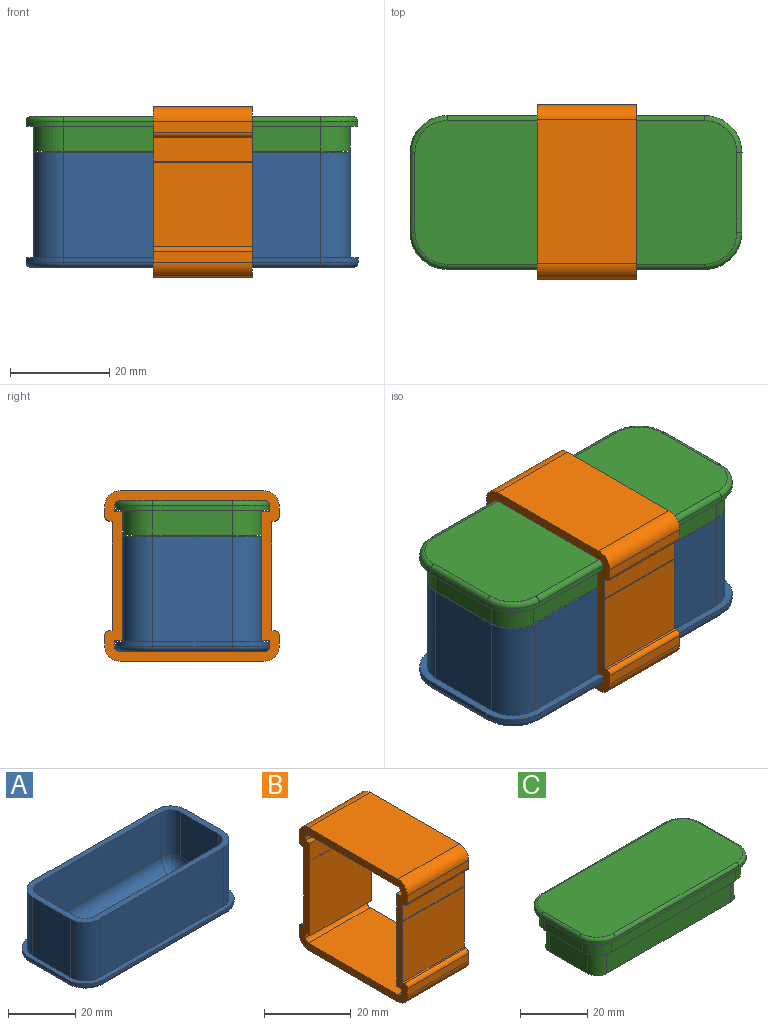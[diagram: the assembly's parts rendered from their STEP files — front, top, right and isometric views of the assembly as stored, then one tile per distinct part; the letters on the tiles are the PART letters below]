
ASSEMBLY  parts=3 mates=5
PART A: 44 faces, bbox 68.3x32.3x23.3 mm
  f0: plane 64.04x28.04mm, normal (0,0,1), area 335.1mm2, adj f1,f2,f3,f4,f5,f6,f7,f8
  f1: cylinder r=4.02mm len=16.3mm, axis (0,0,-1), area 102.9mm2, adj f0,f2,f16,f40
  f2: plane 52x16.3mm, normal (0,-1,0), area 847.6mm2, adj f0,f1,f3,f38
  f3: cylinder r=4.02mm len=16.3mm, axis (0,0,-1), area 102.9mm2, adj f0,f2,f4,f36
  f4: plane 16.3x16mm, normal (1,0,0), area 260.8mm2, adj f0,f3,f5,f37
  f5: cylinder r=4.02mm len=16.3mm, axis (0,0,-1), area 102.9mm2, adj f0,f4,f6,f39
  f6: plane 52x16.3mm, normal (0,1,0), area 847.6mm2, adj f0,f5,f7,f41
  f7: cylinder r=4.02mm len=16.3mm, axis (0,0,-1), area 102.9mm2, adj f0,f6,f16,f43
  f8: cylinder r=6.02mm len=21.3mm, axis (0,0,-1), area 201.4mm2, adj f0,f9,f15,f27
  f9: plane 52x21.3mm, normal (0,1,0), area 1107.6mm2, adj f0,f8,f10,f27
  f10: cylinder r=6.02mm len=21.3mm, axis (0,0,-1), area 201.4mm2, adj f0,f9,f11,f27
  f11: plane 21.3x16mm, normal (1,0,0), area 340.8mm2, adj f0,f10,f12,f27
  f12: cylinder r=6.02mm len=21.3mm, axis (0,0,-1), area 201.4mm2, adj f0,f11,f13,f27
  f13: plane 52x21.3mm, normal (0,-1,0), area 1107.6mm2, adj f0,f12,f14,f27
  f14: cylinder r=6.02mm len=21.3mm, axis (0,0,-1), area 201.4mm2, adj f0,f13,f15,f27
  f15: plane 21.3x16mm, normal (-1,0,0), area 340.8mm2, adj f0,f8,f14,f27
  f16: plane 16.3x16mm, normal (-1,0,0), area 260.8mm2, adj f0,f1,f7,f42
  f17: plane 50.04x14.04mm, normal (0,0,1), area 702.6mm2, adj f37,f38,f41,f42
  f18: cylinder r=7.52mm len=7.52mm, axis (0,0,1), area 11.8mm2, adj f19,f25,f27,f31
  f19: plane 16x1mm, normal (-1,0,0), area 16mm2, adj f18,f20,f27,f29
  f20: cylinder r=7.52mm len=7.52mm, axis (0,0,1), area 11.8mm2, adj f19,f21,f27,f28
  f21: plane 52x1mm, normal (0,1,0), area 52mm2, adj f20,f22,f27,f30
  f22: cylinder r=7.52mm len=7.52mm, axis (0,0,1), area 11.8mm2, adj f21,f23,f27,f32
  f23: plane 16x1mm, normal (1,0,0), area 16mm2, adj f22,f24,f27,f34
  f24: cylinder r=7.52mm len=7.52mm, axis (0,0,1), area 11.8mm2, adj f23,f25,f27,f35
  f25: plane 52x1mm, normal (0,-1,0), area 52mm2, adj f18,f24,f27,f33
  f26: plane 65.04x29.04mm, normal (0,0,-1), area 1852.3mm2, adj f28,f29,f30,f31,f32,f33,f34,f35
  f27: plane 67.04x31.04mm, normal (0,0,1), area 267.8mm2, adj f8,f9,f10,f11,f12,f13,f14,f15
  f28: torus R=6.52mm, axis (0,0,-1), area 17.7mm2, adj f20,f26,f29,f30
  f29: cylinder r=1mm len=16mm, axis (0,-1,0), area 25.1mm2, adj f19,f26,f28,f31
  f30: cylinder r=1mm len=52mm, axis (-1,0,0), area 81.7mm2, adj f21,f26,f28,f32
  f31: torus R=6.52mm, axis (0,0,-1), area 17.7mm2, adj f18,f26,f29,f33
  f32: torus R=6.52mm, axis (0,0,-1), area 17.7mm2, adj f22,f26,f30,f34
  f33: cylinder r=1mm len=52mm, axis (1,0,0), area 81.7mm2, adj f25,f26,f31,f35
  f34: cylinder r=1mm len=16mm, axis (0,1,0), area 25.1mm2, adj f23,f26,f32,f35
  f35: torus R=6.52mm, axis (0,0,-1), area 17.7mm2, adj f24,f26,f33,f34
  f36: bspline ~6.16x5mm, area 32.2mm2, adj f3,f37,f38
  f37: cylinder r=5mm len=16mm, axis (0,-1,0), area 120.1mm2, adj f4,f17,f36,f39
  f38: cylinder r=5mm len=52mm, axis (-1,0,0), area 402.8mm2, adj f2,f17,f36,f40
  f39: bspline ~6.16x5mm, area 32.2mm2, adj f5,f37,f41
  f40: bspline ~6.16x5mm, area 32.2mm2, adj f1,f38,f42
  f41: cylinder r=5mm len=52mm, axis (1,0,0), area 402.8mm2, adj f6,f17,f39,f43
  f42: cylinder r=5mm len=16mm, axis (0,1,0), area 120.1mm2, adj f16,f17,f40,f43
  f43: bspline ~6.16x5mm, area 32.2mm2, adj f7,f41,f42
PART B: 46 faces, bbox 20x35.2x34.5 mm
  f0: cylinder r=1.1mm len=20mm, axis (-1,0,0), area 34.6mm2, adj f1,f37,f38,f39
  f1: plane 20x1.1mm, normal (0,1,0), area 22mm2, adj f0,f2,f38,f39
  f2: plane 20x1.5mm, normal (0,0,-1), area 30mm2, adj f1,f3,f38,f39
  f3: plane 21.1x20mm, normal (0,1,0), area 422mm2, adj f2,f4,f38,f39
  f4: plane 20x0.02mm, normal (0,0,-1), area 0.4mm2, adj f3,f5,f38,f39
  f5: plane 20x5mm, normal (0,1,0), area 100mm2, adj f4,f6,f38,f39
  f6: plane 20x1.5mm, normal (0,0,1), area 30mm2, adj f5,f7,f38,f39
  f7: plane 20x1.1mm, normal (0,1,0), area 22mm2, adj f6,f8,f38,f39
  f8: cylinder r=1.1mm len=20mm, axis (-1,0,0), area 34.6mm2, adj f7,f9,f38,f39
  f9: plane 29x20mm, normal (0,0,-1), area 580mm2, adj f8,f10,f38,f39
  f10: cylinder r=1.1mm len=20mm, axis (-1,0,0), area 34.6mm2, adj f9,f11,f38,f39
  f11: plane 20x1.1mm, normal (0,-1,0), area 22mm2, adj f10,f12,f38,f39
  f12: plane 20x1.5mm, normal (0,0,1), area 30mm2, adj f11,f13,f38,f39
  f13: plane 20x5mm, normal (0,-1,0), area 100mm2, adj f12,f14,f38,f39
  f14: plane 20x0.02mm, normal (0,0,-1), area 0.4mm2, adj f13,f15,f38,f39
  f15: plane 21.1x20mm, normal (0,-1,0), area 422mm2, adj f14,f16,f38,f39
  f16: plane 20x1.5mm, normal (0,0,-1), area 30mm2, adj f15,f17,f38,f39
  f17: plane 20x1.1mm, normal (0,-1,0), area 22mm2, adj f16,f18,f38,f39
  f18: cylinder r=1.1mm len=20mm, axis (-1,0,0), area 34.6mm2, adj f17,f37,f38,f39
  f19: plane 20x0.5mm, normal (0,0,-1), area 10mm2, adj f20,f38,f39,f45
  f20: plane 20x4.8mm, normal (0,-1,0), area 96mm2, adj f19,f38,f39,f40
  f21: plane 20x17.1mm, normal (0,-1,0), area 342mm2, adj f22,f38,f39,f40
  f22: plane 20x0.5mm, normal (0,0,1), area 10mm2, adj f21,f38,f39,f41
  f23: plane 20x2.1mm, normal (0,-1,0), area 42mm2, adj f24,f38,f39,f41
  f24: cylinder r=3.1mm len=20mm, axis (-1,0,0), area 97.4mm2, adj f23,f25,f38,f39
  f25: plane 29.04x20mm, normal (0,0,-1), area 580.8mm2, adj f24,f26,f38,f39
  f26: cylinder r=3.1mm len=20mm, axis (-1,0,0), area 97.4mm2, adj f25,f27,f38,f39
  f27: plane 20x2.1mm, normal (0,1,0), area 42mm2, adj f26,f38,f39,f42
  f28: plane 20x0.5mm, normal (0,0,1), area 10mm2, adj f29,f38,f39,f42
  f29: plane 20x17.1mm, normal (0,1,0), area 342mm2, adj f28,f38,f39,f43
  f30: plane 20x4.8mm, normal (0,1,0), area 96mm2, adj f31,f38,f39,f43
  f31: plane 20x0.5mm, normal (0,0,-1), area 10mm2, adj f30,f38,f39,f44
  f32: plane 20x2.1mm, normal (0,1,0), area 42mm2, adj f33,f38,f39,f44
  f33: cylinder r=3.1mm len=20mm, axis (-1,0,0), area 97.4mm2, adj f32,f34,f38,f39
  f34: plane 29x20mm, normal (0,0,1), area 580mm2, adj f33,f35,f38,f39
  f35: cylinder r=3.1mm len=20mm, axis (-1,0,0), area 97.4mm2, adj f34,f36,f38,f39
  f36: plane 20x2.1mm, normal (0,-1,0), area 42mm2, adj f35,f38,f39,f45
  f37: plane 29.04x20mm, normal (0,0,1), area 580.8mm2, adj f0,f18,f38,f39
  f38: plane 35.24x34.5mm, normal (1,0,0), area 266.7mm2, adj f0,f1,f2,f3,f4,f5,f6,f7
  f39: plane 35.24x34.5mm, normal (-1,0,0), area 266.7mm2, adj f0,f1,f2,f3,f4,f5,f6,f7
  f40: cylinder r=1mm len=20mm, axis (1,0,0), area 4mm2, adj f20,f21,f38,f39
  f41: cylinder r=1mm len=20mm, axis (-1,0,0), area 31.4mm2, adj f22,f23,f38,f39
  f42: cylinder r=1mm len=20mm, axis (1,0,0), area 31.4mm2, adj f27,f28,f38,f39
  f43: cylinder r=1mm len=20mm, axis (-1,0,0), area 4mm2, adj f29,f30,f38,f39
  f44: cylinder r=1mm len=20mm, axis (-1,0,0), area 31.4mm2, adj f31,f32,f38,f39
  f45: cylinder r=1mm len=20mm, axis (1,0,0), area 31.4mm2, adj f19,f36,f38,f39
PART C: 60 faces, bbox 68.2x32.2x15.8 mm
  f0: plane 16x8.8mm, normal (1,0,0), area 140.8mm2, adj f1,f7,f20,f41
  f1: cylinder r=4mm len=8.8mm, axis (0,0,-1), area 55.3mm2, adj f0,f2,f20,f41
  f2: plane 52x8.8mm, normal (0,1,0), area 457.6mm2, adj f1,f3,f20,f41
  f3: cylinder r=4mm len=8.8mm, axis (0,0,-1), area 55.3mm2, adj f2,f4,f20,f41
  f4: plane 16x8.8mm, normal (-1,0,0), area 140.8mm2, adj f3,f5,f20,f41
  f5: cylinder r=4mm len=8.8mm, axis (0,0,-1), area 55.3mm2, adj f4,f6,f20,f41
  f6: plane 52x8.8mm, normal (0,-1,0), area 457.6mm2, adj f5,f7,f20,f41
  f7: cylinder r=4mm len=8.8mm, axis (0,0,-1), area 55.3mm2, adj f0,f6,f20,f41
  f8: cylinder r=3.65mm len=12.8mm, axis (0,0,-1), area 293.6mm2, adj f20,f21
  f9: cylinder r=3.65mm len=12.8mm, axis (0,0,-1), area 293.6mm2, adj f20,f22
  f10: cylinder r=3.65mm len=12.8mm, axis (0,0,-1), area 293.6mm2, adj f20,f23
  f11: cylinder r=3.65mm len=12.8mm, axis (0,0,-1), area 293.6mm2, adj f20,f24
  f12: cylinder r=3.65mm len=12.8mm, axis (0,0,-1), area 293.6mm2, adj f20,f25
  f13: cylinder r=3.65mm len=12.8mm, axis (0,0,-1), area 293.6mm2, adj f20,f26
  f14: cylinder r=3.65mm len=12.8mm, axis (0,0,-1), area 293.6mm2, adj f20,f27
  f15: cylinder r=3.65mm len=12.8mm, axis (0,0,-1), area 293.6mm2, adj f20,f28
  f16: cylinder r=3.65mm len=12.8mm, axis (0,0,-1), area 293.6mm2, adj f20,f29
  f17: cylinder r=3.65mm len=12.8mm, axis (0,0,-1), area 293.6mm2, adj f20,f30
  f18: cylinder r=3.65mm len=12.8mm, axis (0,0,-1), area 293.6mm2, adj f20,f31
  f19: cylinder r=3.65mm len=12.8mm, axis (0,0,-1), area 293.6mm2, adj f20,f32
  f20: plane 60x24mm, normal (0,0,-1), area 924mm2, adj f0,f1,f2,f3,f4,f5,f6,f7
  f21: plane 7.3x7.3mm, normal (0,0,-1), area 41.9mm2, adj f8
  f22: plane 7.3x7.3mm, normal (0,0,-1), area 41.9mm2, adj f9
  f23: plane 7.3x7.3mm, normal (0,0,-1), area 41.9mm2, adj f10
  f24: plane 7.3x7.3mm, normal (0,0,-1), area 41.9mm2, adj f11
  f25: plane 7.3x7.3mm, normal (0,0,-1), area 41.9mm2, adj f12
  f26: plane 7.3x7.3mm, normal (0,0,-1), area 41.9mm2, adj f13
  f27: plane 7.3x7.3mm, normal (0,0,-1), area 41.9mm2, adj f14
  f28: plane 7.3x7.3mm, normal (0,0,-1), area 41.9mm2, adj f15
  f29: plane 7.3x7.3mm, normal (0,0,-1), area 41.9mm2, adj f16
  f30: plane 7.3x7.3mm, normal (0,0,-1), area 41.9mm2, adj f17
  f31: plane 7.3x7.3mm, normal (0,0,-1), area 41.9mm2, adj f18
  f32: plane 7.3x7.3mm, normal (0,0,-1), area 41.9mm2, adj f19
  f33: cylinder r=6mm len=6mm, axis (0,0,1), area 47.1mm2, adj f34,f40,f41,f51
  f34: plane 16x5mm, normal (1,0,0), area 80mm2, adj f33,f35,f41,f51
  f35: cylinder r=6mm len=6mm, axis (0,0,1), area 47.1mm2, adj f34,f36,f41,f51
  f36: plane 52x5mm, normal (0,-1,0), area 260mm2, adj f35,f37,f41,f51
  f37: cylinder r=6mm len=6mm, axis (0,0,1), area 47.1mm2, adj f36,f38,f41,f51
  f38: plane 16x5mm, normal (-1,0,0), area 80mm2, adj f37,f39,f41,f51
  f39: cylinder r=6mm len=6mm, axis (0,0,1), area 47.1mm2, adj f38,f40,f41,f51
  f40: plane 52x5mm, normal (0,1,0), area 260mm2, adj f33,f39,f41,f51
  f41: plane 64x28mm, normal (0,0,-1), area 334.8mm2, adj f0,f1,f2,f3,f4,f5,f6,f7
  f42: plane 65x29mm, normal (0,0,1), area 1848.7mm2, adj f52,f53,f54,f55,f56,f57,f58,f59
  f43: cylinder r=7.5mm len=7.5mm, axis (0,0,1), area 11.8mm2, adj f44,f50,f51,f54
  f44: plane 52x1mm, normal (0,-1,0), area 52mm2, adj f43,f45,f51,f52
  f45: cylinder r=7.5mm len=7.5mm, axis (0,0,1), area 11.8mm2, adj f44,f46,f51,f53
  f46: plane 16x1mm, normal (1,0,0), area 16mm2, adj f45,f47,f51,f55
  f47: cylinder r=7.5mm len=7.5mm, axis (0,0,1), area 11.8mm2, adj f46,f48,f51,f57
  f48: plane 52x1mm, normal (0,1,0), area 52mm2, adj f47,f49,f51,f59
  f49: cylinder r=7.5mm len=7.5mm, axis (0,0,1), area 11.8mm2, adj f48,f50,f51,f58
  f50: plane 16x1mm, normal (-1,0,0), area 16mm2, adj f43,f49,f51,f56
  f51: plane 67x31mm, normal (0,0,-1), area 267.6mm2, adj f33,f34,f35,f36,f37,f38,f39,f40
  f52: cylinder r=1mm len=52mm, axis (1,0,0), area 81.7mm2, adj f42,f44,f53,f54
  f53: torus R=6.5mm, axis (0,0,1), area 17.6mm2, adj f42,f45,f52,f55
  f54: torus R=6.5mm, axis (0,0,1), area 17.6mm2, adj f42,f43,f52,f56
  f55: cylinder r=1mm len=16mm, axis (0,1,0), area 25.1mm2, adj f42,f46,f53,f57
  f56: cylinder r=1mm len=16mm, axis (0,-1,0), area 25.1mm2, adj f42,f50,f54,f58
  f57: torus R=6.5mm, axis (0,0,1), area 17.6mm2, adj f42,f47,f55,f59
  f58: torus R=6.5mm, axis (0,0,1), area 17.6mm2, adj f42,f49,f56,f59
  f59: cylinder r=1mm len=52mm, axis (-1,0,0), area 81.7mm2, adj f42,f48,f57,f58
PLACE A t=(-14.1,3.83,-35.15)mm
PLACE B t=(-53.96,3.93,-35.05)mm
PLACE C t=(-14.12,3.81,-34.95)mm
MATE planar C.f6 <-> A.f6  axis (0,-1,0) through (-14.12,-8.19,-30.55)mm
MATE planar B.f9 <-> C.f42  axis (0,0,-1) through (-1.94,-10.57,-19.15)mm
MATE planar A.f13 <-> B.f3  axis (0,-1,0) through (-40.1,-10.19,-37)mm
MATE planar A.f26 <-> B.f37  axis (0,0,-1) through (-14.1,3.83,-49.65)mm
MATE planar A.f4 <-> C.f4  axis (1,0,0) through (-44.12,3.83,-26.35)mm
